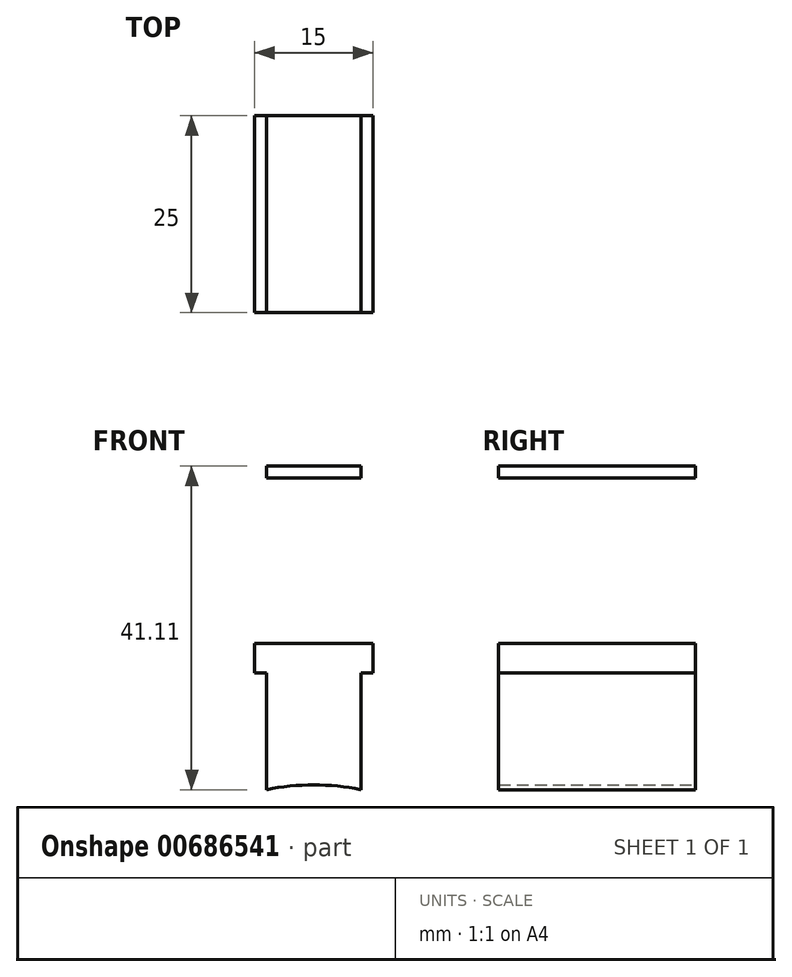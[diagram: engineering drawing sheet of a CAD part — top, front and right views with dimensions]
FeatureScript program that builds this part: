
annotation { "Feature Type Name" : "Feature", "Feature Type Description" : "" }
export const myFeature = defineFeature(function(context is Context, id is Id, definition is map)
    precondition{}
    {
        {
            var Q0;
            Q0=qCreatedBy(makeId("Front.planeOp"),FACE);
            var sketch = newSketch(context, id + "F0", { "sketchPlane" : qUnion([Q0])});
            skCircle(sketch, "E0", {"center": v(0, 0) * mm, "radius": 30 * mm});
            skPoint(sketch, "E1", {"position": v(-6, 0) * mm});
            skCircle(sketch, "E2", {"center": v(-6, 0) * mm, "radius": 12 * mm});
            skLineSegment(sketch, "E3", {"start": v(6, 69) * mm, "end": v(-6, 69) * mm});
            skLineSegment(sketch, "E4", {"start": v(-6, 69) * mm, "end": v(-6, 29.4) * mm});
            skLineSegment(sketch, "E5", {"start": v(6, 29.4) * mm, "end": v(6, 69) * mm});
            skLineSegment(sketch, "E6.bottom", {"start": v(-7.5, 48) * mm, "end": v(7.5, 48) * mm});
            skLineSegment(sketch, "E6.top", {"start": v(-7.5, 44.25) * mm, "end": v(7.5, 44.25) * mm});
            skLineSegment(sketch, "E6.left", {"start": v(-7.5, 48) * mm, "end": v(-7.5, 44.25) * mm});
            skLineSegment(sketch, "E6.right", {"start": v(7.5, 48) * mm, "end": v(7.5, 44.25) * mm});
            skLineSegment(sketch, "E7", {"start": v(74.84, 0) * mm, "end": v(-75.29, 0) * mm, "construction": true});
            skPoint(sketch, "E8.startSnap0", {"position": v(0, 69) * mm});
            skLineSegment(sketch, "E9.bottom", {"start": v(-6, 70.5) * mm, "end": v(6, 70.5) * mm});
            skLineSegment(sketch, "E9.top", {"start": v(-6, 69) * mm, "end": v(6, 69) * mm});
            skLineSegment(sketch, "E9.left", {"start": v(-6, 70.5) * mm, "end": v(-6, 69) * mm});
            skLineSegment(sketch, "E9.right", {"start": v(6, 70.5) * mm, "end": v(6, 69) * mm});
            skPoint(sketch, "E10.visualSharp", {"position": v(-6, 70.5) * mm});
            skLineSegment(sketch, "E10.filletArc", {"start": v(-6, 70.5) * mm, "end": v(-6, 70.5) * mm});
            skSolve(sketch);
        }
        {
            var Q0;
            {var subQ5=sQuery(id+"F0.wireOp",EDGE,"E6.right");Q0=makeQuery(id+"F0.imprint","IMPRINT",FACE,{"disambiguationData":[TD([[makeQuery(id+"F0.imprint","IMPRINT",EDGE,{"derivedFrom":subQ5}),-1.0]])]});}
            var Q1;
            {var subQ5=sQuery(id+"F0.wireOp",EDGE,"E6.left");Q1=makeQuery(id+"F0.imprint","IMPRINT",FACE,{"disambiguationData":[TD([[makeQuery(id+"F0.imprint","IMPRINT",EDGE,{"derivedFrom":subQ5}),1.0]])]});}
            var Q2;
            Q2=makeQuery(id+"F0.imprint","IMPRINT",FACE,{"disambiguationData":[TD([[makeQuery(id+"F0.imprint","IMPRINT",EDGE,{"derivedFrom":sQuery(id+"F0.wireOp",EDGE,"E9.bottom")}),-1.0]])]});
            var Q3;
            {var subQ0=sQuery(id+"F0.wireOp",EDGE,"E9.top");Q3=makeQuery(id+"F0.imprint","IMPRINT",FACE,{"disambiguationData":[TD([[makeQuery(id+"F0.imprint","IMPRINT",EDGE,{"derivedFrom":subQ0}),-1.0]])]});}
            var Q4;
            {var subQ0=sQuery(id+"F0.wireOp",EDGE,"E6.bottom");var subQ1=sQuery(id+"F0.wireOp",EDGE,"E4");var subQ2=makeQuery(id+"F0.imprint","INTERSECT",VERTEX,{"derivedFrom":[subQ1,subQ0]});Q4=makeQuery(id+"F0.imprint","IMPRINT",FACE,{"disambiguationData":[TD([[makeQuery(id+"F0.imprint","IMPRINT",EDGE,{"disambiguationData":[TD([[subQ2,-1.0]])],"derivedFrom":subQ1}),1.0]])]});}
            var Q5;
            {var subQ0=sQuery(id+"F0.wireOp",EDGE,"E4");var subQ1=sQuery(id+"F0.wireOp",EDGE,"E0");var subQ2=makeQuery(id+"F0.imprint","INTERSECT",VERTEX,{"derivedFrom":[subQ1,subQ0]});Q5=makeQuery(id+"F0.imprint","IMPRINT",FACE,{"disambiguationData":[TD([[makeQuery(id+"F0.imprint","IMPRINT",EDGE,{"disambiguationData":[TD([[subQ2,1.0]])],"derivedFrom":subQ1}),-1.0]])]});}
            extrude(context, id + "F1", {"entities" : qUnion([Q0, Q1, Q2, Q3, Q4, Q5]), "depth" : 25 * mm, "offsetDistance" : 25 * mm});
        }
    });
